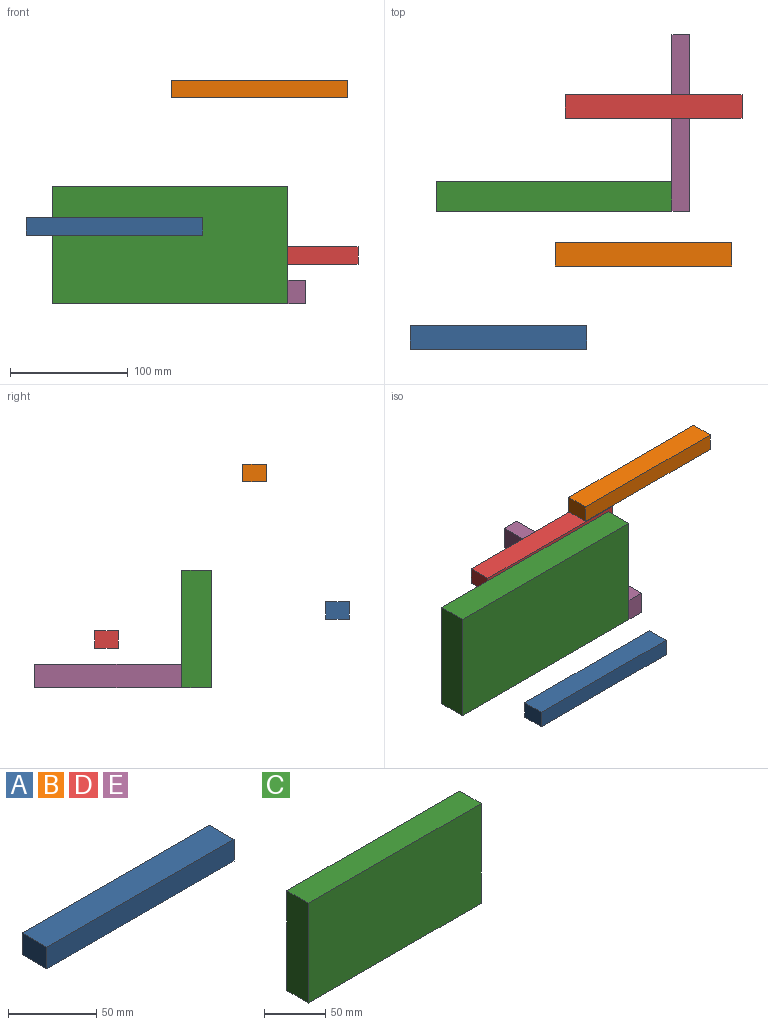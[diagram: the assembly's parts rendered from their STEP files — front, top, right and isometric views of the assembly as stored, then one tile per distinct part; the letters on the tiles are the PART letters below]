
ASSEMBLY  parts=5 mates=1
PART A: 6 faces, bbox 150x20x15 mm
  f0: plane 150x15mm, normal (0,-1,0), area 2250mm2, adj f1,f3,f4,f5
  f1: plane 20x15mm, normal (1,0,0), area 300mm2, adj f0,f2,f4,f5
  f2: plane 150x15mm, normal (0,1,0), area 2250mm2, adj f1,f3,f4,f5
  f3: plane 20x15mm, normal (-1,0,0), area 300mm2, adj f0,f2,f4,f5
  f4: plane 150x20mm, normal (0,0,1), area 3000mm2, adj f0,f1,f2,f3
  f5: plane 150x20mm, normal (0,0,-1), area 3000mm2, adj f0,f1,f2,f3
PART B: same geometry as A
PART C: 6 faces, bbox 200x25x100 mm
  f0: plane 200x25mm, normal (0,0,1), area 5000mm2, adj f1,f3,f4,f5
  f1: plane 100x25mm, normal (-1,0,0), area 2500mm2, adj f0,f2,f4,f5
  f2: plane 200x25mm, normal (0,0,-1), area 5000mm2, adj f1,f3,f4,f5
  f3: plane 100x25mm, normal (1,0,0), area 2500mm2, adj f0,f2,f4,f5
  f4: plane 200x100mm, normal (0,-1,0), area 20000mm2, adj f0,f1,f2,f3
  f5: plane 200x100mm, normal (0,1,0), area 20000mm2, adj f0,f1,f2,f3
PART D: same geometry as A
PART E: same geometry as A
PLACE A t=(-106.8,-261.25,85.44)mm
PLACE B t=(16.7,-190.8,202.17)mm
PLACE C t=(-69.79,-74.77,57.52)mm
PLACE D t=(25.26,-65.01,60.69)mm
PLACE E rot(axis=(-0.58,-0.58,0.58),120deg) t=(71.5,-40.5,91.32)mm
MATE revolute E.f3 <-> C.f4  axis (0,-1,0) through (56.5,-99.77,27.05)mm
